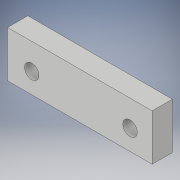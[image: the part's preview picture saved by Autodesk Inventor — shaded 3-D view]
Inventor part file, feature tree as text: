
AUTODESK INVENTOR PART (.ipt)
format: ipt  version: 2017 (Build 210142000, 142)  size: 98,304 bytes
history: native  units: in
note: dims shown in document units (in); Inventor stores cm internally (conversion verified against a paired STEP export)
features: sketch x2, extrude x1, hole x1
ambient origin geometry x8: Origin, YZ Plane, XZ Plane, XY Plane, X Axis, Y Axis, Z Axis, Center Point
bodies: Solid1 (feature_tree)
feature tree (4):
  extrude  "Extrusion1"  Depth=0.6299in
  hole  "Hole1"  [1 undecoded]
  sketch  "Sketch1"  dims[d0=1.9685in d1=0.6299in]
  sketch  "Sketch2"  dims[d2=0.2756in d3=0.0in d4=0.2756in d5=0.2756in d6=1.3386in d7=0.1969in d8=0.2362in d9=0.1575in d10=0.0787in d11=90.0deg d12=0.315in d13=0.8108in]
note: 1 required parameter value undecoded (feature->parameter linkage not recoverable at this tier; creation-order binding heuristic only, values carry confidence <= 0.55)
